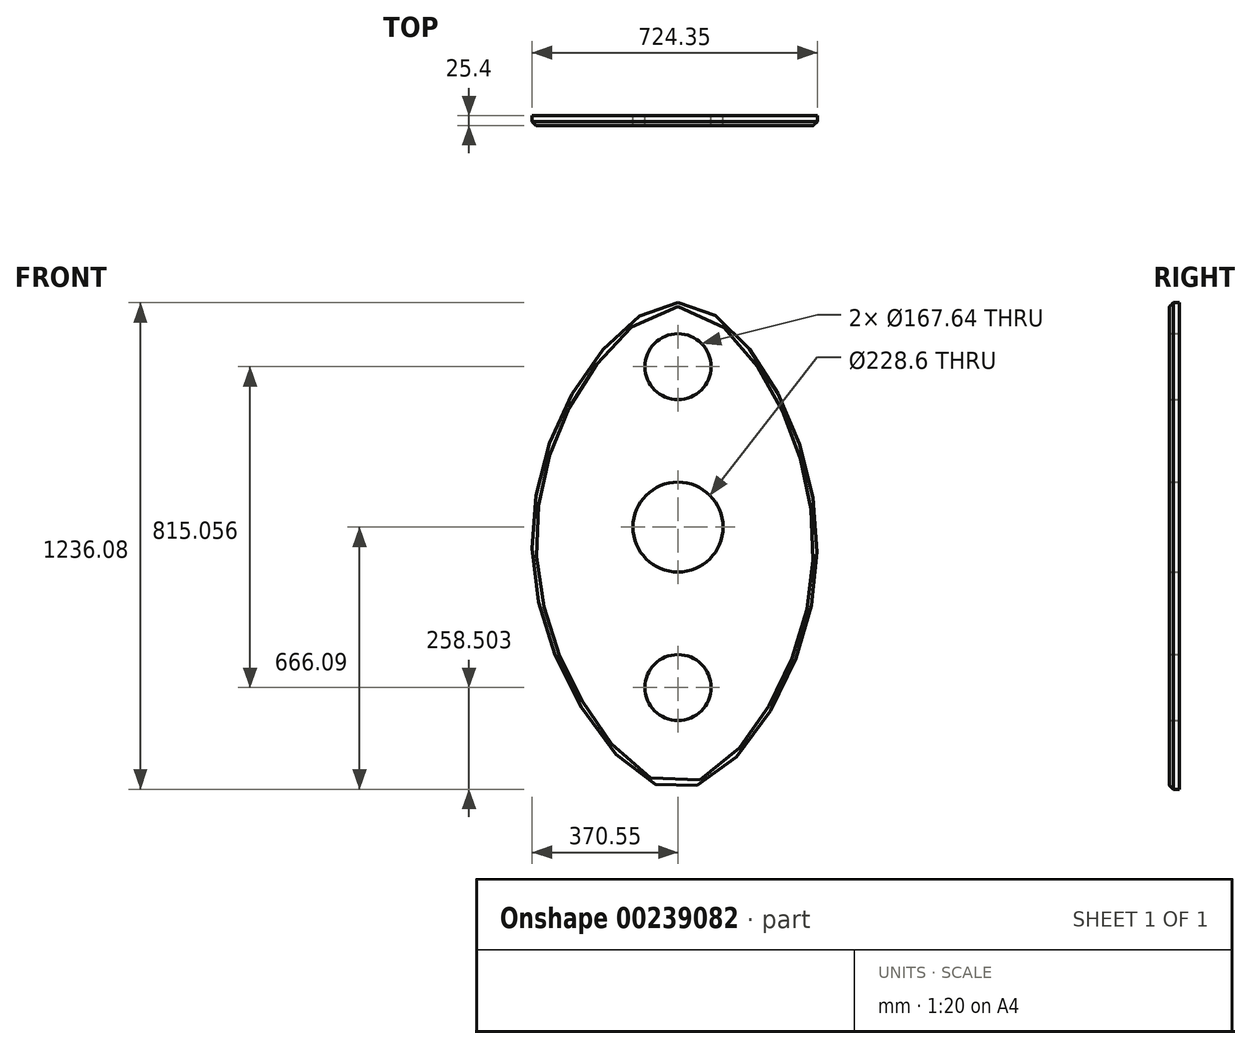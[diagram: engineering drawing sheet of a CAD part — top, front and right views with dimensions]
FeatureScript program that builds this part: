
annotation { "Feature Type Name" : "Feature", "Feature Type Description" : "" }
export const myFeature = defineFeature(function(context is Context, id is Id, definition is map)
    precondition{}
    {
        {
            var Q0;
            Q0=qCreatedBy(makeId("Front.planeOp"),FACE);
            var sketch = newSketch(context, id + "F0", { "sketchPlane" : qUnion([Q0])});
            skLineSegment(sketch, "E0", {"start": v(0, 0) * mm, "end": v(0, 407.47) * mm});
            skLineSegment(sketch, "E1", {"start": v(0, 0) * mm, "end": v(0, -407.59) * mm});
            skCircle(sketch, "E2", {"center": v(0, 407.47) * mm, "radius": 83.82 * mm});
            skCircle(sketch, "E3", {"center": v(0, -407.59) * mm, "radius": 83.82 * mm});
            skCircle(sketch, "E4", {"center": v(0, 0) * mm, "radius": 114.3 * mm});
            skFitSpline(sketch, "E5", {"points": [v(0, 570) * mm, v(-238.84, 386.35) * mm, v(-369.6, 0) * mm, v(-269.2, -416.84) * mm, v(0, -666.09) * mm, v(263.15, -416.84) * mm, v(351.87, 0) * mm, v(218.78, 400.36) * mm, v(0, 570) * mm]});
            skSolve(sketch);
        }
        {
            var Q0;
            Q0=makeQuery(id+"F0.imprint","IMPRINT",FACE,{"disambiguationData":[TD([[makeQuery(id+"F0.imprint","IMPRINT",EDGE,{"derivedFrom":sQuery(id+"F0.wireOp",EDGE,"E2")}),-1.0]])]});
            extrude(context, id + "F1", {"entities" : qUnion([Q0]), "depth" : 25.4 * mm});
        }
        {
            var Q0;
            Q0=makeQuery(id+"F1.opExtrude","CAP_EDGE",EDGE,{"disambiguationData":[OSD([sQuery(id+"F0.wireOp",EDGE,"E5")])],"isStart":false});
            chamfer(context, id + "F2", {"entities" : qUnion([Q0]), "width" : 10 * mm, "tangentPropagation" : true});
        }
    });
